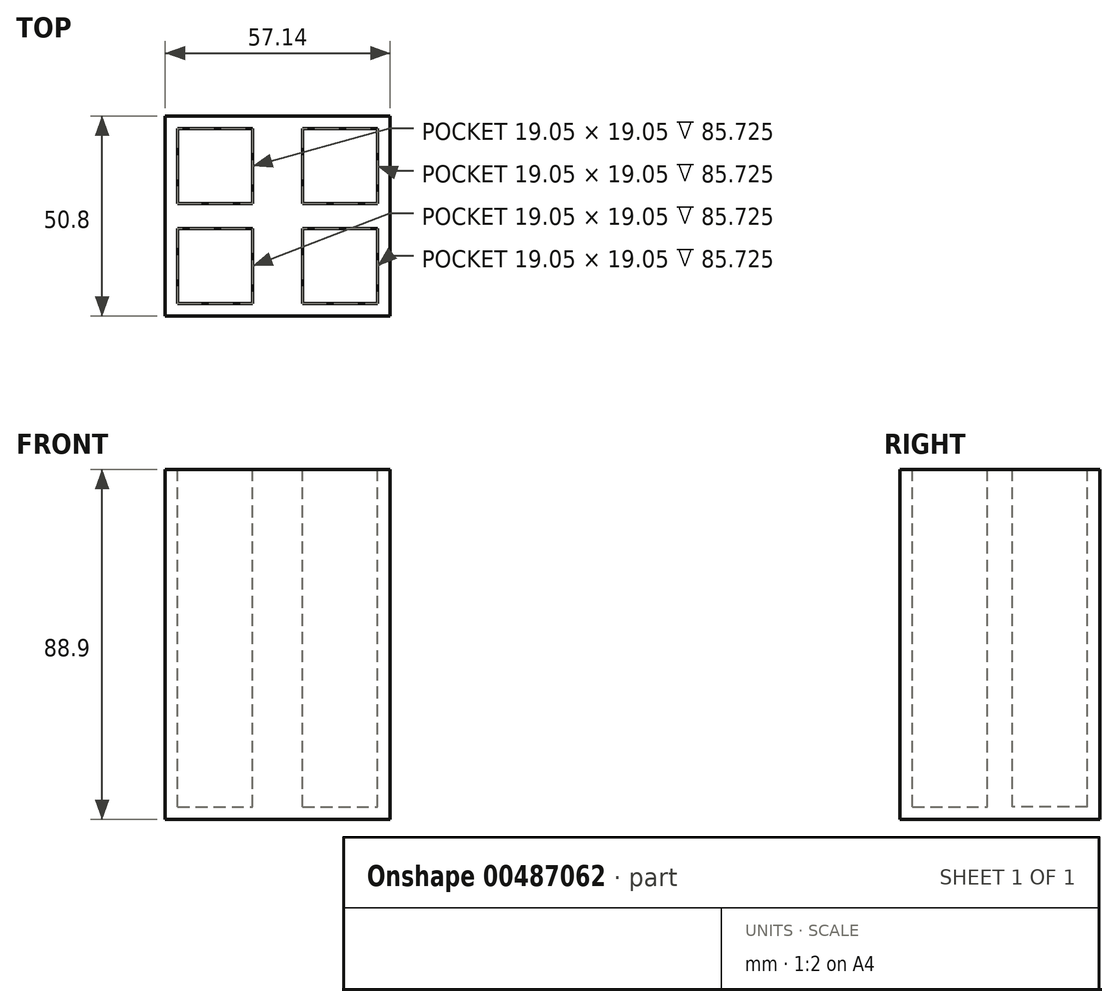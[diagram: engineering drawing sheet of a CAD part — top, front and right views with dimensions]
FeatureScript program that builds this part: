
annotation { "Feature Type Name" : "Feature", "Feature Type Description" : "" }
export const myFeature = defineFeature(function(context is Context, id is Id, definition is map)
    precondition{}
    {
        {
            var Q0;
            Q0=qCreatedBy(makeId("Front.planeOp"),FACE);
            var sketch = newSketch(context, id + "F0", { "sketchPlane" : qUnion([Q0])});
            skLineSegment(sketch, "E0.bottom", {"start": v(-28.58, 44.45) * mm, "end": v(28.58, 44.45) * mm});
            skLineSegment(sketch, "E0.top", {"start": v(-28.58, -44.45) * mm, "end": v(28.58, -44.45) * mm});
            skLineSegment(sketch, "E0.left", {"start": v(-28.58, 44.45) * mm, "end": v(-28.58, -44.45) * mm});
            skLineSegment(sketch, "E0.right", {"start": v(28.58, 44.45) * mm, "end": v(28.58, -44.45) * mm});
            skPoint(sketch, "E0.middle", {"position": v(0, 0) * mm});
            skSolve(sketch);
        }
        {
            var Q0;
            Q0=makeQuery(id+"F0.imprint","IMPRINT",FACE,{"disambiguationData":[TD([[makeQuery(id+"F0.imprint","IMPRINT",EDGE,{"derivedFrom":sQuery(id+"F0.wireOp",EDGE,"E0.bottom")}),-1.0]])]});
            extrude(context, id + "F1", {"entities" : qUnion([Q0]), "depth" : 50.8 * mm});
        }
        {
            var Q0;
            Q0=makeQuery(id+"F1.opExtrude","SWEPT_FACE",FACE,{"disambiguationData":[OSD([sQuery(id+"F0.wireOp",EDGE,"E0.bottom")])]});
            var sketch = newSketch(context, id + "F2", { "sketchPlane" : qUnion([Q0])});
            skLineSegment(sketch, "E1.bottom", {"start": v(-25.4, -3.17) * mm, "end": v(-6.35, -3.17) * mm});
            skLineSegment(sketch, "E1.top", {"start": v(-25.4, -22.22) * mm, "end": v(-6.35, -22.22) * mm});
            skLineSegment(sketch, "E1.left", {"start": v(-25.4, -3.17) * mm, "end": v(-25.4, -22.22) * mm});
            skLineSegment(sketch, "E1.right", {"start": v(-6.35, -3.17) * mm, "end": v(-6.35, -22.22) * mm});
            skSolve(sketch);
        }
        {
            var Q0;
            Q0=makeQuery(id+"F1.opExtrude","SWEPT_FACE",FACE,{"disambiguationData":[OSD([sQuery(id+"F0.wireOp",EDGE,"E0.bottom")])]});
            var sketch = newSketch(context, id + "F3", { "sketchPlane" : qUnion([Q0])});
            skLineSegment(sketch, "E2.bottom", {"start": v(6.35, -22.23) * mm, "end": v(25.4, -22.23) * mm});
            skLineSegment(sketch, "E2.top", {"start": v(6.35, -3.18) * mm, "end": v(25.4, -3.18) * mm});
            skLineSegment(sketch, "E2.left", {"start": v(6.35, -22.23) * mm, "end": v(6.35, -3.18) * mm});
            skLineSegment(sketch, "E2.right", {"start": v(25.4, -22.23) * mm, "end": v(25.4, -3.18) * mm});
            skSolve(sketch);
        }
        {
            var Q0;
            Q0=makeQuery(id+"F1.opExtrude","SWEPT_FACE",FACE,{"disambiguationData":[OSD([sQuery(id+"F0.wireOp",EDGE,"E0.bottom")])]});
            var sketch = newSketch(context, id + "F4", { "sketchPlane" : qUnion([Q0])});
            skLineSegment(sketch, "E3.bottom", {"start": v(25.4, -47.63) * mm, "end": v(6.35, -47.63) * mm});
            skLineSegment(sketch, "E3.top", {"start": v(25.4, -28.58) * mm, "end": v(6.35, -28.58) * mm});
            skLineSegment(sketch, "E3.left", {"start": v(25.4, -47.63) * mm, "end": v(25.4, -28.58) * mm});
            skLineSegment(sketch, "E3.right", {"start": v(6.35, -47.63) * mm, "end": v(6.35, -28.58) * mm});
            skSolve(sketch);
        }
        {
            var Q0;
            Q0=makeQuery(id+"F1.opExtrude","SWEPT_FACE",FACE,{"disambiguationData":[OSD([sQuery(id+"F0.wireOp",EDGE,"E0.bottom")])]});
            var sketch = newSketch(context, id + "F5", { "sketchPlane" : qUnion([Q0])});
            skLineSegment(sketch, "E4.bottom", {"start": v(-25.4, -47.63) * mm, "end": v(-6.35, -47.63) * mm});
            skLineSegment(sketch, "E4.top", {"start": v(-25.4, -28.58) * mm, "end": v(-6.35, -28.58) * mm});
            skLineSegment(sketch, "E4.left", {"start": v(-25.4, -47.63) * mm, "end": v(-25.4, -28.58) * mm});
            skLineSegment(sketch, "E4.right", {"start": v(-6.35, -47.63) * mm, "end": v(-6.35, -28.58) * mm});
            skSolve(sketch);
        }
        {
            var Q0;
            Q0=makeQuery(id+"F2.imprint","IMPRINT",FACE,{"disambiguationData":[TD([[makeQuery(id+"F2.imprint","IMPRINT",EDGE,{"derivedFrom":sQuery(id+"F2.wireOp",EDGE,"E1.bottom")}),-1.0]])]});
            extrude(context, id + "F6", {"entities" : qUnion([Q0]), "operationType" : NewBodyOperationType.REMOVE, "oppositeDirection" : true, "depth" : 85.72 * mm});
        }
        {
            var Q0;
            Q0=makeQuery(id+"F3.imprint","IMPRINT",FACE,{"disambiguationData":[TD([[makeQuery(id+"F3.imprint","IMPRINT",EDGE,{"derivedFrom":sQuery(id+"F3.wireOp",EDGE,"E2.bottom")}),1.0]])]});
            extrude(context, id + "F7", {"entities" : qUnion([Q0]), "operationType" : NewBodyOperationType.REMOVE, "oppositeDirection" : true, "depth" : 85.72 * mm});
        }
        {
            var Q0;
            Q0=makeQuery(id+"F5.imprint","IMPRINT",FACE,{"disambiguationData":[TD([[makeQuery(id+"F5.imprint","IMPRINT",EDGE,{"derivedFrom":sQuery(id+"F5.wireOp",EDGE,"E4.bottom")}),1.0]])]});
            extrude(context, id + "F8", {"entities" : qUnion([Q0]), "operationType" : NewBodyOperationType.REMOVE, "oppositeDirection" : true, "depth" : 85.72 * mm});
        }
        {
            var Q0;
            Q0=makeQuery(id+"F4.imprint","IMPRINT",FACE,{"disambiguationData":[TD([[makeQuery(id+"F4.imprint","IMPRINT",EDGE,{"derivedFrom":sQuery(id+"F4.wireOp",EDGE,"E3.bottom")}),-1.0]])]});
            extrude(context, id + "F9", {"entities" : qUnion([Q0]), "operationType" : NewBodyOperationType.REMOVE, "oppositeDirection" : true, "depth" : 85.72 * mm});
        }
    });
